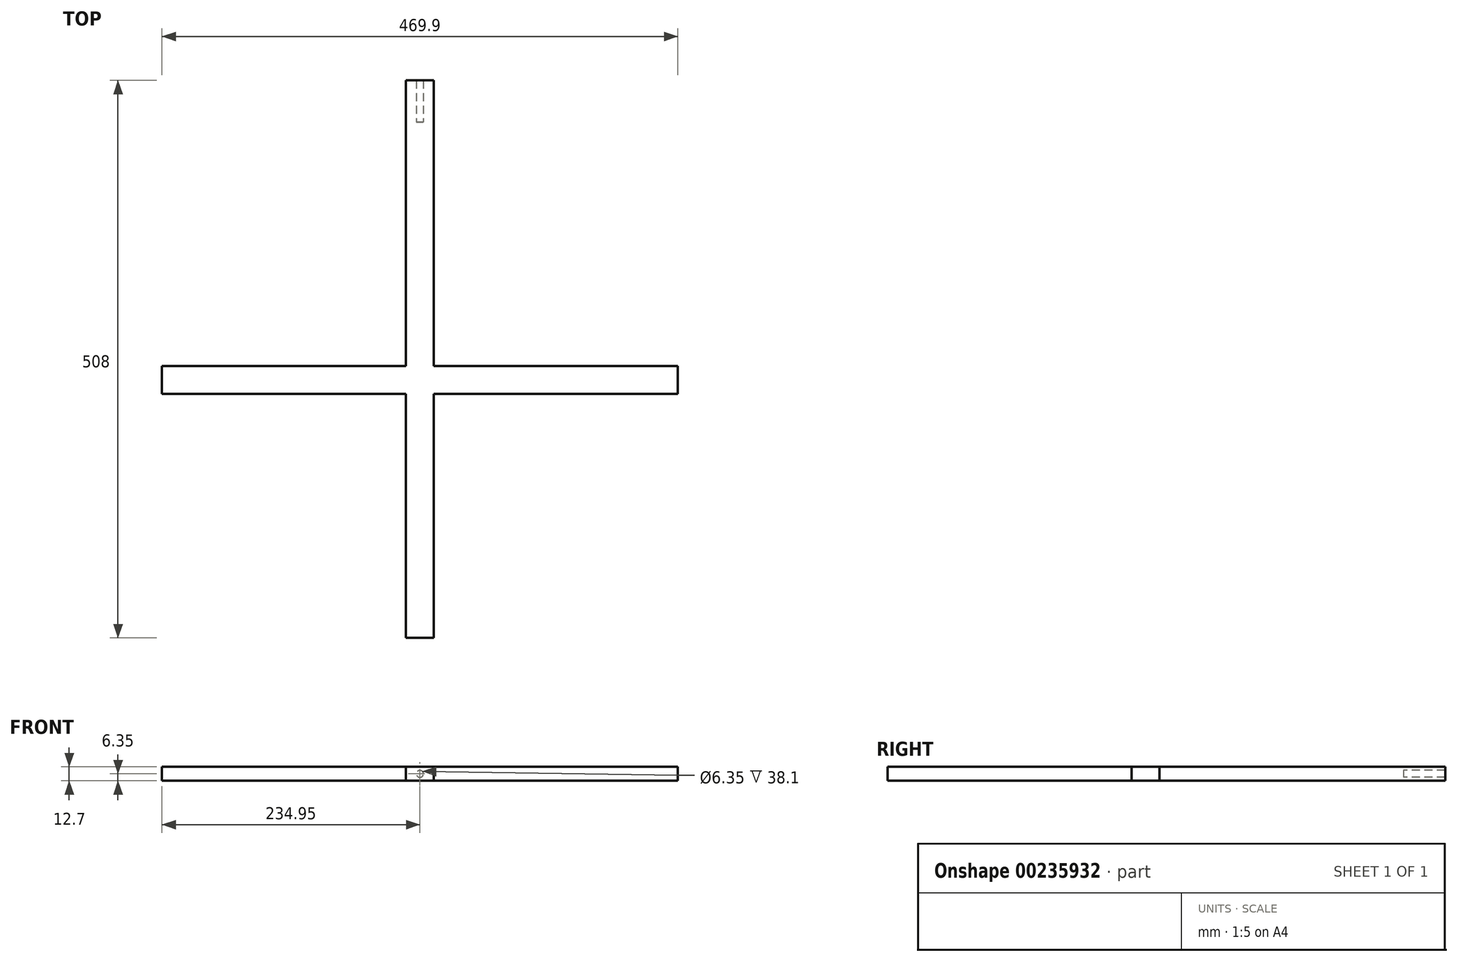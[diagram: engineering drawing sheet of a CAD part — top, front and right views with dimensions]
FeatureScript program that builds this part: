
annotation { "Feature Type Name" : "Feature", "Feature Type Description" : "" }
export const myFeature = defineFeature(function(context is Context, id is Id, definition is map)
    precondition{}
    {
        {
            var Q0;
            Q0=qCreatedBy(makeId("Top.planeOp"),FACE);
            var sketch = newSketch(context, id + "F0", { "sketchPlane" : qUnion([Q0])});
            skLineSegment(sketch, "E0.bottom", {"start": v(0, 0) * mm, "end": v(-25.4, 0) * mm});
            skLineSegment(sketch, "E0.top", {"start": v(0, 469.9) * mm, "end": v(-25.4, 469.9) * mm});
            skLineSegment(sketch, "E0.right", {"start": v(-25.4, 0) * mm, "end": v(-25.4, 222.25) * mm});
            skLineSegment(sketch, "E1", {"start": v(0, 469.9) * mm, "end": v(0, 247.65) * mm});
            skLineSegment(sketch, "E2", {"start": v(-25.4, 222.25) * mm, "end": v(-247.65, 222.25) * mm});
            skLineSegment(sketch, "E3", {"start": v(-25.4, 247.65) * mm, "end": v(-247.65, 247.65) * mm});
            skLineSegment(sketch, "E4", {"start": v(0, 222.25) * mm, "end": v(222.25, 222.25) * mm});
            skLineSegment(sketch, "E5", {"start": v(0, 247.65) * mm, "end": v(222.25, 247.65) * mm});
            skLineSegment(sketch, "E6", {"start": v(-247.65, 247.65) * mm, "end": v(-247.65, 222.25) * mm});
            skLineSegment(sketch, "E7", {"start": v(222.25, 247.65) * mm, "end": v(222.25, 222.25) * mm});
            skLineSegment(sketch, "E8.trimOffspring", {"start": v(0, 222.25) * mm, "end": v(0, 0) * mm});
            skLineSegment(sketch, "E9.trimOffspring", {"start": v(-25.4, 247.65) * mm, "end": v(-25.4, 469.9) * mm});
            skSolve(sketch);
        }
        {
            var Q0;
            Q0=makeQuery(id+"F0.imprint","IMPRINT",FACE,{"disambiguationData":[TD([[makeQuery(id+"F0.imprint","IMPRINT",EDGE,{"derivedFrom":sQuery(id+"F0.wireOp",EDGE,"E0.bottom")}),-1.0]])]});
            extrude(context, id + "F1", {"entities" : qUnion([Q0]), "depth" : 12.7 * mm});
        }
        {
            var Q0;
            Q0=makeQuery(id+"F1.opExtrude","SWEPT_FACE",FACE,{"disambiguationData":[OSD([sQuery(id+"F0.wireOp",EDGE,"E0.bottom")])]});
            var sketch = newSketch(context, id + "F2", { "sketchPlane" : qUnion([Q0])});
            skPoint(sketch, "E10.orphan", {"position": v(0, 6.35) * mm});
            skPoint(sketch, "E11.orphan", {"position": v(-12.7, 0) * mm});
            skPoint(sketch, "E12", {"position": v(-12.7, 6.35) * mm});
            skCircle(sketch, "E13", {"center": v(-12.7, 6.35) * mm, "radius": 3.18 * mm});
            skSolve(sketch);
        }
        {
            var Q0;
            Q0=makeQuery(id+"F1.opExtrude","SWEPT_FACE",FACE,{"disambiguationData":[OSD([sQuery(id+"F0.wireOp",EDGE,"E0.top")])]});
            var sketch = newSketch(context, id + "F3", { "sketchPlane" : qUnion([Q0])});
            skCircle(sketch, "E14.0", {"center": v(12.7, 6.35) * mm, "radius": 3.18 * mm});
            skSolve(sketch);
        }
        {
            var Q0;
            Q0=makeQuery(id+"F3.imprint","IMPRINT",FACE,{"disambiguationData":[TD([[makeQuery(id+"F3.imprint","IMPRINT",EDGE,{"derivedFrom":sQuery(id+"F3.wireOp",EDGE,"E14.0")}),-1.0]])]});
            extrude(context, id + "F4", {"entities" : qUnion([Q0]), "operationType" : NewBodyOperationType.ADD, "depth" : 38.1 * mm});
        }
    });
